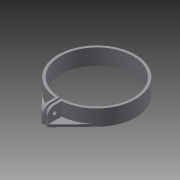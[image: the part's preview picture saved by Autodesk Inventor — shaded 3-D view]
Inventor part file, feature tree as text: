
AUTODESK INVENTOR PART (.ipt)
format: ipt  version: 2013 (Build 170138000, 138)  size: 134,656 bytes
history: native  units: mm
features: extrude x4, sketch x4, fillet x2
ambient origin geometry x8: Origin, YZ Plane, XZ Plane, XY Plane, X Axis, Y Axis, Z Axis, Center Point
bodies: Solid1 (feature_tree)
feature tree (10):
  extrude  "Extrusion1"  Depth=2.0mm
  extrude  "Extrusion2"  Depth=1.5mm
  extrude  "Extrusion3"  Depth=11.2mm TaperAngle=0.0deg
  extrude  "Extrusion4"  Depth=10.0mm TaperAngle=0.0deg
  fillet  "Fillet1"  Radius=2.0mm
  fillet  "Fillet2"  Radius=2.0mm
  sketch  "Sketch1"  dims[d0=60.325mm d2=2.0mm]
  sketch  "Sketch2"  dims[d3=2.0mm d4=1.5mm]
  sketch  "Sketch3"  dims[d5=11.4mm d6=11.2mm d7=0.0mm]
  sketch  "Sketch4"  dims[d8=3.2mm d10=10.0mm d11=0.0mm d12=2.0mm d13=0.0mm d14=2.0mm d15=0.0mm d16=5.5mm d17=1.0mm]
